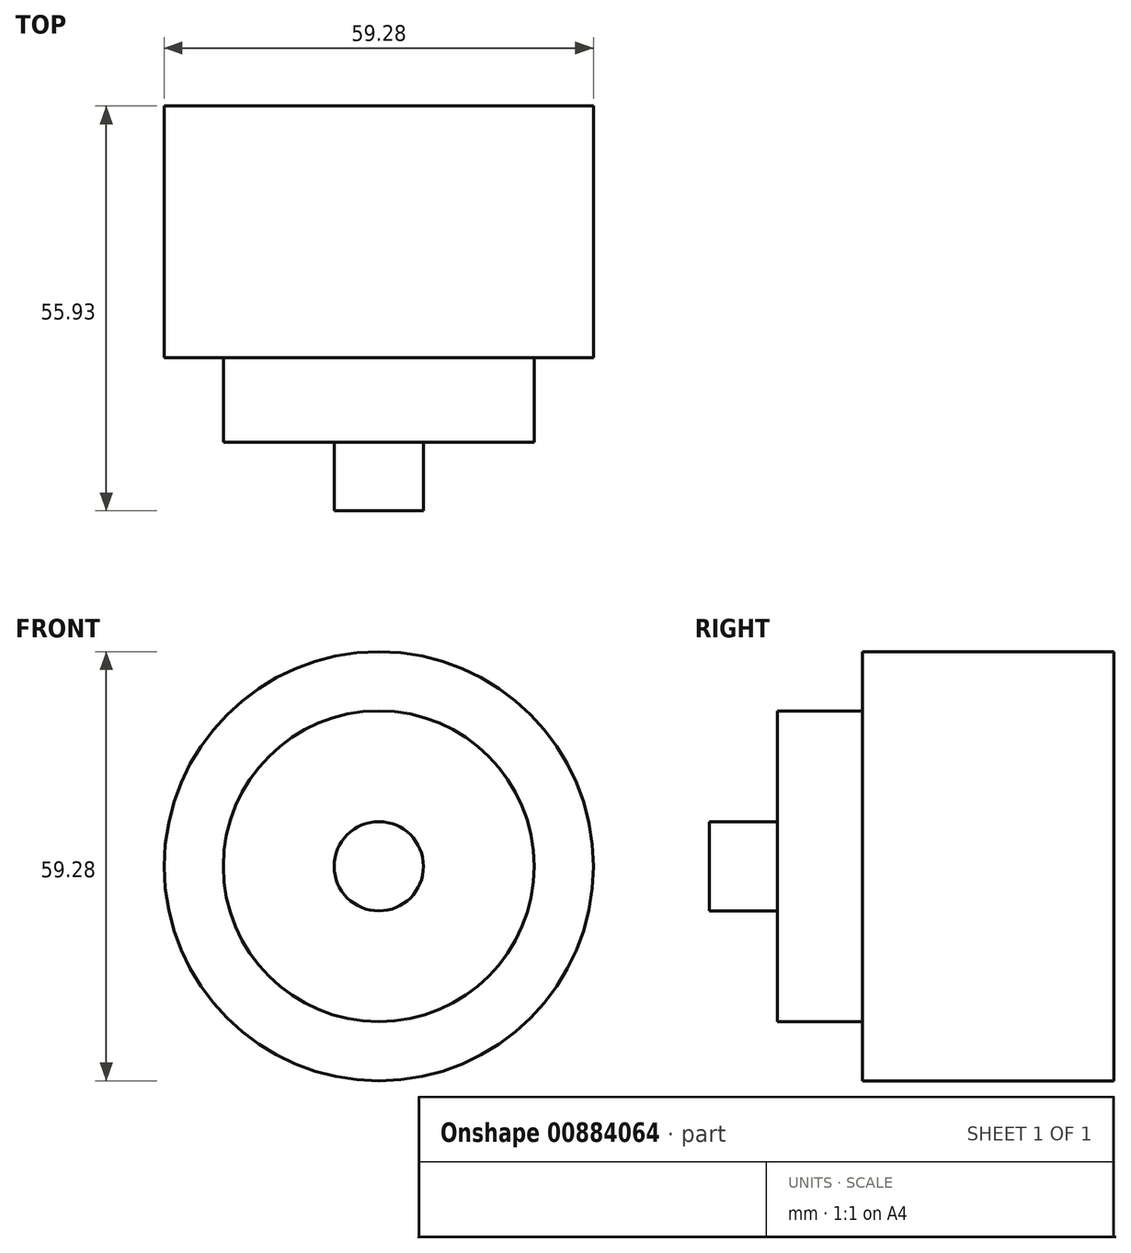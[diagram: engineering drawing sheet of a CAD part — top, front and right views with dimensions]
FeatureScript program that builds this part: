
annotation { "Feature Type Name" : "Feature", "Feature Type Description" : "" }
export const myFeature = defineFeature(function(context is Context, id is Id, definition is map)
    precondition{}
    {
        {
            var Q0;
            Q0=qCreatedBy(makeId("Right.planeOp"),FACE);
            var sketch = newSketch(context, id + "F0", { "sketchPlane" : qUnion([Q0])});
            skLineSegment(sketch, "E0", {"start": v(0, -29.64) * mm, "end": v(-34.76, -29.64) * mm});
            skLineSegment(sketch, "E1", {"start": v(-34.76, -29.64) * mm, "end": v(-34.76, -21.48) * mm});
            skLineSegment(sketch, "E2", {"start": v(-34.76, -21.48) * mm, "end": v(-46.5, -21.48) * mm});
            skLineSegment(sketch, "E3", {"start": v(-46.5, -21.48) * mm, "end": v(-46.5, -6.17) * mm});
            skLineSegment(sketch, "E4", {"start": v(-46.5, -6.17) * mm, "end": v(-55.93, -6.17) * mm});
            skLineSegment(sketch, "E5", {"start": v(-55.93, -6.17) * mm, "end": v(-55.93, 0) * mm});
            skLineSegment(sketch, "E6", {"start": v(0, -29.64) * mm, "end": v(0, 0) * mm});
            skLineSegment(sketch, "E7", {"start": v(-69.45, 0) * mm, "end": v(11.68, 0) * mm});
            skSolve(sketch);
        }
        {
            var Q0;
            Q0=sQuery(id+"F0.wireOp",EDGE,"E5");
            var Q1;
            Q1=sQuery(id+"F0.wireOp",EDGE,"E4");
            var Q2;
            Q2=sQuery(id+"F0.wireOp",EDGE,"E3");
            var Q3;
            Q3=sQuery(id+"F0.wireOp",EDGE,"E2");
            var Q4;
            Q4=sQuery(id+"F0.wireOp",EDGE,"E1");
            var Q5;
            Q5=sQuery(id+"F0.wireOp",EDGE,"E0");
            var Q6;
            Q6=sQuery(id+"F0.wireOp",EDGE,"E6");
            var Q7;
            Q7=sQuery(id+"F0.wireOp",EDGE,"E7");
            revolve(context, id + "F1", {"bodyType" : ToolBodyType.SURFACE, "surfaceOperationType" : NewSurfaceOperationType.NEW, "surfaceEntities" : qUnion([Q0, Q1, Q2, Q3, Q4, Q5, Q6]), "axis" : qUnion([Q7]), "revolveType" : RevolveType.FULL});
        }
    });
